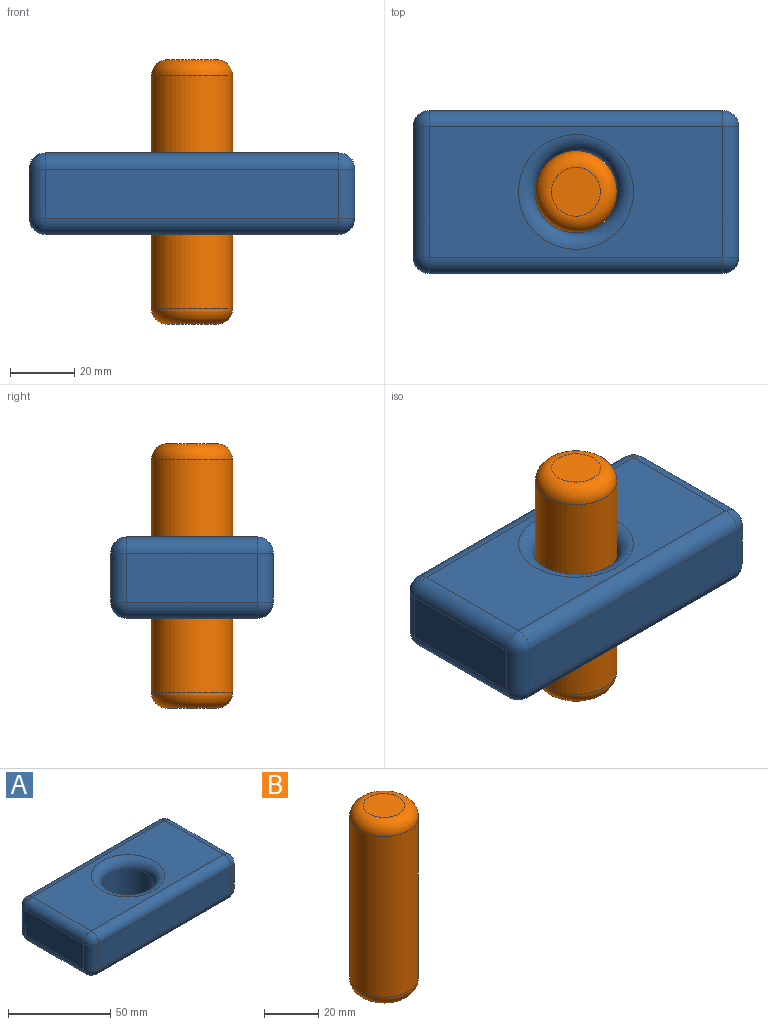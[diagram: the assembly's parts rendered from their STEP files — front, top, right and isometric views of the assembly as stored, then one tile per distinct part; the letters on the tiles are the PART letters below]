
ASSEMBLY  parts=2 mates=1
PART A: 29 faces, bbox 101.6x50.8x25.4 mm
  f0: plane 40.64x15.24mm, normal (-1,0,0), area 619.4mm2, adj f15,f20,f23,f26
  f1: plane 91.44x15.24mm, normal (0,-1,0), area 1393.5mm2, adj f12,f21,f22,f26
  f2: plane 40.64x15.24mm, normal (1,0,0), area 619.4mm2, adj f7,f11,f12,f13
  f3: plane 91.44x15.24mm, normal (0,1,0), area 1393.5mm2, adj f7,f10,f14,f15
  f4: cylinder r=12.83mm len=25.65mm, axis (0,0,-1), area 1228.3mm2, adj f27,f28
  f5: plane 91.44x40.64mm, normal (0,0,1), area 2708.7mm2, adj f10,f11,f20,f21,f28
  f6: plane 91.44x40.64mm, normal (0,0,-1), area 2708.7mm2, adj f13,f14,f22,f23,f27
  f7: cylinder r=5.08mm len=15.24mm, axis (0,0,1), area 121.6mm2, adj f2,f3,f8,f9
  f8: sphere r=5.08mm, area 40.5mm2, adj f7,f10,f11
  f9: sphere r=5.08mm, area 40.5mm2, adj f7,f13,f14
  f10: cylinder r=5.08mm len=91.44mm, axis (1,0,0), area 729.7mm2, adj f3,f5,f8,f16
  f11: cylinder r=5.08mm len=40.64mm, axis (0,-1,0), area 324.3mm2, adj f2,f5,f8,f17
  f12: cylinder r=5.08mm len=15.24mm, axis (0,0,-1), area 121.6mm2, adj f1,f2,f17,f18
  f13: cylinder r=5.08mm len=40.64mm, axis (0,1,0), area 324.3mm2, adj f2,f6,f9,f18
  f14: cylinder r=5.08mm len=91.44mm, axis (-1,0,0), area 729.7mm2, adj f3,f6,f9,f19
  f15: cylinder r=5.08mm len=15.24mm, axis (0,0,-1), area 121.6mm2, adj f0,f3,f16,f19
  f16: sphere r=5.08mm, area 40.5mm2, adj f10,f15,f20
  f17: sphere r=5.08mm, area 40.5mm2, adj f11,f12,f21
  f18: sphere r=5.08mm, area 40.5mm2, adj f12,f13,f22
  f19: sphere r=5.08mm, area 40.5mm2, adj f14,f15,f23
  f20: cylinder r=5.08mm len=40.64mm, axis (0,1,0), area 324.3mm2, adj f0,f5,f16,f24
  f21: cylinder r=5.08mm len=91.44mm, axis (-1,0,0), area 729.7mm2, adj f1,f5,f17,f24
  f22: cylinder r=5.08mm len=91.44mm, axis (1,0,0), area 729.7mm2, adj f1,f6,f18,f25
  f23: cylinder r=5.08mm len=40.64mm, axis (0,-1,0), area 324.3mm2, adj f0,f6,f19,f25
  f24: sphere r=5.08mm, area 40.5mm2, adj f20,f21,f26
  f25: sphere r=5.08mm, area 40.5mm2, adj f22,f23,f26
  f26: cylinder r=5.08mm len=15.24mm, axis (0,0,1), area 121.6mm2, adj f0,f1,f24,f25
  f27: torus R=17.91mm, axis (0,0,1), area 735.7mm2, adj f4,f6
  f28: torus R=17.91mm, axis (0,0,1), area 735.7mm2, adj f4,f5
PART B: 5 faces, bbox 27.5x27.5x82.6 mm
  f0: cylinder r=12.7mm len=72.39mm, axis (0,0,-1), area 5776.5mm2, adj f3,f4
  f1: plane 15.24x15.24mm, normal (0,0,1), area 182.4mm2, adj f4
  f2: plane 15.24x15.24mm, normal (0,0,-1), area 182.4mm2, adj f3
  f3: torus R=7.62mm, axis (0,0,1), area 544.2mm2, adj f0,f2
  f4: torus R=7.62mm, axis (0,0,1), area 544.2mm2, adj f0,f1
PLACE A at identity
PLACE B t=(4.34,2.66,-28.07)mm
MATE slider B.f0 <-> A.f4  axis (0,0,-1) through (4.34,2.66,13.21)mm
